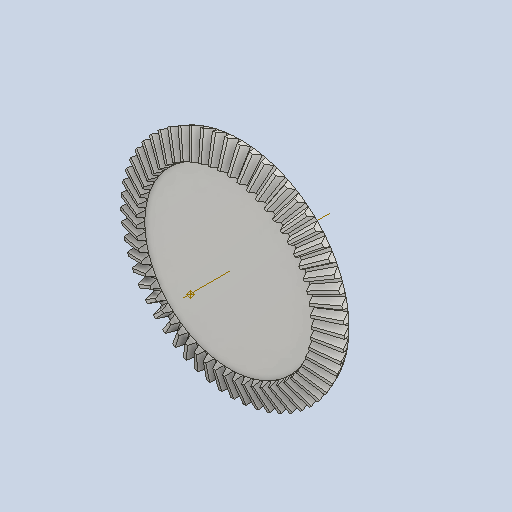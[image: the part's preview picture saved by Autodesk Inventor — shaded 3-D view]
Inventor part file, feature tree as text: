
AUTODESK INVENTOR PART (.ipt)
format: ipt  version: 2024 (Build 280153000, 153)  size: 859,648 bytes
history: native  units: mm
features: other x24, loft x2, pattern_circular x2
ambient origin geometry x6: Origin, XZ Plane, X Axis, Y Axis, Z Axis, Center Point
bodies: Solid1 (feature_tree)
feature tree (28):
  other  "Top Point"
  other  "Mesh Plane2"
  other  "Teeth Body"
  other  "Start Point"
  other  "Tooth Plane"
  other  "Start Sketch"
  other  "End Point"
  other  "3D Sketch Right"
  other  "End Plane Right"
  loft  "Loft Right"
  pattern_circular  "Circular Pattern Right"  [2 undecoded]
  other  "3D Sketch Left"
  other  "End Plane Left"
  loft  "Loft Left"
  pattern_circular  "Circular Pattern Left"  Count=2  [1 undecoded]
  other  "Fix Body"
  other  "Mesh Plane"
  other  "Top Plane"
  other  "Teeth Body Sketch"
  other  "End Plane"
  other  "End Sketch"
  other  "Helical Curve Left"
  other  "End Sketch Left"
  other  "Body Sketch"
  other  "Srf1"
  other  "Helical Curve Right"
  other  "End Sketch Right"
  other  "Pitch Diameter"
note: 3 required parameter values undecoded (feature->parameter linkage not recoverable at this tier; creation-order binding heuristic only, values carry confidence <= 0.55)
